# Revit family: MixerTap_Shower_Nero_Celia_Rectangular_Backplate
name_source: partatom
category: Plumbing Fixtures
units: mm (PartAtom-declared; Revit-internal decimal feet)

## family parameters
Always vertical = Yes
Cut with Voids When Loaded = Yes
Maintain Annotation Orientation = No
OmniClass Number = 23.31.11.19
OmniClass Title = Faucet Mixing Valves
Part Type = Normal
Room Calculation Point = No
Round Connector Dimension = Use Diameter
Shared = No
Work Plane-Based = No

## types (3) — shared parameters
Assembly Code = D2010
CW Connection = Yes
Default Elevation = 1050 mm
HW Connection = Yes
IfcExportAs = IfcValve
IfcExportType = MIXING
Manufacturer = Nero
ManufacturerOverallDepth = 58.6 mm
ManufacturerOverallHeight = 150 mm
ManufacturerOverallWidth = 65 mm  [stored 0.213255 ft]
ModifiedIssue = 20251009 $
URL = https://nerotapware.com.au
Uniclass2015Code = Pr_40_20_87
Uniclass2015Title = Taps and water supply outlet fittings
Uniclass2015Version = Products v1.35
Vent Connection = No
Waste Connection = No
zero-valued in all types: CWFU, HWFU, WFU

## per-type parameters (varying)
| type | Description | ManufacturerSpecCode | Material | Model | Type Comments |
| Chrome (NR301511bCH) | Celia Shower Mixer Rectangular Backplate Chrome | NR301511bCH | Metal_Chrome_Nero | NR301511bCH | Mixer Tap - Shower - Rectangular - Backplate - Chrome |
| Matte Black (NR301511bMB) | Celia Shower Mixer Rectangular Backplate Matte Black | NR301511bMB | Metal_MatteBlack_Nero | NR301511bMB | Mixer Tap - Shower - Rectangular - Backplate - Matte Black |
| Brushed Nickel (NR301511bBN) | Celia Shower Mixer Rectangular Backplate Brushed Nickel | NR301511bBN | Metal_Nickel_Nero_Brushed | NR301511bBN | Mixer Tap - Shower - Rectangular - Backplate - Brushed Nickel |

note: [stored X ft] marks values corroborated as IEEE doubles in the binary element streams (Revit-internal decimal feet)

## geometry (parser evidence)
native form markers: Sweep x2
no freeform markers — native parametric forms only
